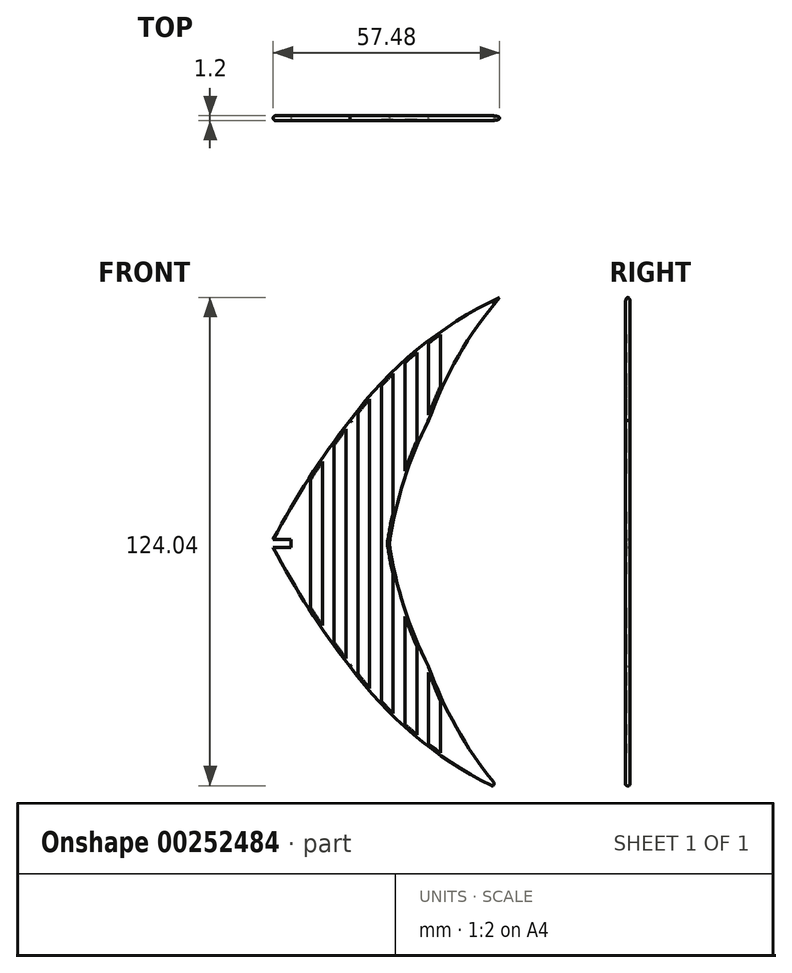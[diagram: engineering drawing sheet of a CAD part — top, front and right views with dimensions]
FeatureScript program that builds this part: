
annotation { "Feature Type Name" : "Feature", "Feature Type Description" : "" }
export const myFeature = defineFeature(function(context is Context, id is Id, definition is map)
    precondition{}
    {
        {
            var Q0;
            Q0=qCreatedBy(makeId("Front.planeOp"),FACE);
            var sketch = newSketch(context, id + "F0", { "sketchPlane" : qUnion([Q0])});
            skLineSegment(sketch, "E0", {"start": v(0, 0) * mm, "end": v(30, 0) * mm});
            skLineSegment(sketch, "E1", {"start": v(20, 31.25) * mm, "end": v(40, 31.25) * mm});
            skPoint(sketch, "E2", {"position": v(58, 62.5) * mm});
            skArc(sketch, "E3", {"start": v(20, 31.25) * mm, "mid": v(9.27, 16.09) * mm, "end": v(0, 0) * mm});
            skArc(sketch, "E4", {"start": v(58, 62.5) * mm, "mid": v(37.05, 49.25) * mm, "end": v(20, 31.25) * mm});
            skArc(sketch, "E5", {"start": v(58, 62.5) * mm, "mid": v(47.58, 47.7) * mm, "end": v(40, 31.25) * mm});
            skArc(sketch, "E6", {"start": v(40, 31.25) * mm, "mid": v(33.7, 16.04) * mm, "end": v(30, 0) * mm});
            skSolve(sketch);
        }
        {
            var Q0;
            Q0=qSketchRegion(id+"F0",true);
            extrude(context, id + "F1", {"entities" : qUnion([Q0]), "endBound" : BoundingType.SYMMETRIC, "depth" : 1.2 * mm});
        }
        {
            var Q0;
            Q0=makeQuery(id+"F1.opExtrude","SWEPT_BODY",BODY,{"disambiguationData":[OSD([sQuery(id+"F0.wireOp",EDGE,"E0"),sQuery(id+"F0.wireOp",EDGE,"E3"),sQuery(id+"F0.wireOp",EDGE,"E4"),sQuery(id+"F0.wireOp",EDGE,"E5"),sQuery(id+"F0.wireOp",EDGE,"E6")])]});
            var Q1;
            Q1=qCreatedBy(makeId("Top.planeOp"),FACE);
            mirror(context, id + "F2", {"operationType" : NewBodyOperationType.ADD, "entities" : qUnion([Q0]), "mirrorPlane" : qUnion([Q1])});
        }
        {
            var Q0;
            Q0=qCreatedBy(makeId("Front.planeOp"),FACE);
            var sketch = newSketch(context, id + "F3", { "sketchPlane" : qUnion([Q0])});
            skLineSegment(sketch, "E7.bottom", {"start": v(5, -1) * mm, "end": v(-5, -1) * mm});
            skLineSegment(sketch, "E7.top", {"start": v(5, 1) * mm, "end": v(-5, 1) * mm});
            skLineSegment(sketch, "E7.left", {"start": v(5, -1) * mm, "end": v(5, 1) * mm});
            skLineSegment(sketch, "E7.right", {"start": v(-5, -1) * mm, "end": v(-5, 1) * mm});
            skPoint(sketch, "E7.middle", {"position": v(0, 0) * mm});
            skSolve(sketch);
        }
        {
            var Q0;
            Q0=makeQuery(id+"F3.imprint","IMPRINT",FACE,{"disambiguationData":[TD([[makeQuery(id+"F3.imprint","IMPRINT",EDGE,{"derivedFrom":sQuery(id+"F3.wireOp",EDGE,"E7.bottom")}),-1.0]])]});
            extrude(context, id + "F4", {"entities" : qUnion([Q0]), "operationType" : NewBodyOperationType.REMOVE, "endBound" : BoundingType.SYMMETRIC, "oppositeDirection" : true, "depth" : 5 * mm});
        }
        {
            var Q0;
            Q0=makeQuery(id+"F1.opExtrude","CAP_EDGE",EDGE,{"disambiguationData":[OSD([sQuery(id+"F0.wireOp",EDGE,"E4")])],"isStart":false});
            var Q1;
            Q1=makeQuery(id+"F1.opExtrude","CAP_EDGE",EDGE,{"disambiguationData":[OSD([sQuery(id+"F0.wireOp",EDGE,"E4")])],"isStart":true});
            var Q2;
            Q2=makeQuery(id+"F1.opExtrude","CAP_EDGE",EDGE,{"disambiguationData":[OSD([sQuery(id+"F0.wireOp",EDGE,"E3")])],"isStart":false});
            var Q3;
            Q3=makeQuery(id+"F1.opExtrude","CAP_EDGE",EDGE,{"disambiguationData":[OSD([sQuery(id+"F0.wireOp",EDGE,"E3")])],"isStart":true});
            var Q4;
            Q4=makeQuery(id+"F1.opExtrude","CAP_EDGE",EDGE,{"disambiguationData":[OSD([sQuery(id+"F0.wireOp",EDGE,"E5")])],"isStart":false});
            var Q5;
            Q5=makeQuery(id+"F1.opExtrude","CAP_EDGE",EDGE,{"disambiguationData":[OSD([sQuery(id+"F0.wireOp",EDGE,"E5")])],"isStart":true});
            var Q6;
            Q6=makeQuery(id+"F1.opExtrude","CAP_EDGE",EDGE,{"disambiguationData":[OSD([sQuery(id+"F0.wireOp",EDGE,"E6")])],"isStart":false});
            var Q7;
            Q7=makeQuery(id+"F1.opExtrude","CAP_EDGE",EDGE,{"disambiguationData":[OSD([sQuery(id+"F0.wireOp",EDGE,"E6")])],"isStart":true});
            var Q8;
            Q8=makeQuery(id+"F2.opPattern","COPY",EDGE,{"derivedFrom":makeQuery(id+"F1.opExtrude","CAP_EDGE",EDGE,{"disambiguationData":[OSD([sQuery(id+"F0.wireOp",EDGE,"E3")])],"isStart":false}),"instanceName":"1"});
            var Q9;
            Q9=makeQuery(id+"F2.opPattern","COPY",EDGE,{"derivedFrom":makeQuery(id+"F1.opExtrude","CAP_EDGE",EDGE,{"disambiguationData":[OSD([sQuery(id+"F0.wireOp",EDGE,"E3")])],"isStart":true}),"instanceName":"1"});
            var Q10;
            Q10=makeQuery(id+"F2.opPattern","COPY",EDGE,{"derivedFrom":makeQuery(id+"F1.opExtrude","CAP_EDGE",EDGE,{"disambiguationData":[OSD([sQuery(id+"F0.wireOp",EDGE,"E4")])],"isStart":false}),"instanceName":"1"});
            var Q11;
            Q11=makeQuery(id+"F2.opPattern","COPY",EDGE,{"derivedFrom":makeQuery(id+"F1.opExtrude","CAP_EDGE",EDGE,{"disambiguationData":[OSD([sQuery(id+"F0.wireOp",EDGE,"E4")])],"isStart":true}),"instanceName":"1"});
            var Q12;
            Q12=makeQuery(id+"F2.opPattern","COPY",EDGE,{"derivedFrom":makeQuery(id+"F1.opExtrude","CAP_EDGE",EDGE,{"disambiguationData":[OSD([sQuery(id+"F0.wireOp",EDGE,"E6")])],"isStart":false}),"instanceName":"1"});
            var Q13;
            Q13=makeQuery(id+"F2.opPattern","COPY",FACE,{"derivedFrom":makeQuery(id+"F1.opExtrude","SWEPT_FACE",FACE,{"disambiguationData":[OSD([sQuery(id+"F0.wireOp",EDGE,"E6")])]}),"instanceName":"1"});
            var Q14;
            Q14=makeQuery(id+"F2.opPattern","COPY",EDGE,{"derivedFrom":makeQuery(id+"F1.opExtrude","CAP_EDGE",EDGE,{"disambiguationData":[OSD([sQuery(id+"F0.wireOp",EDGE,"E5")])],"isStart":false}),"instanceName":"1"});
            var Q15;
            Q15=makeQuery(id+"F2.opPattern","COPY",FACE,{"derivedFrom":makeQuery(id+"F1.opExtrude","SWEPT_FACE",FACE,{"disambiguationData":[OSD([sQuery(id+"F0.wireOp",EDGE,"E5")])]}),"instanceName":"1"});
            fillet(context, id + "F5", {"entities" : qUnion([Q0, Q1, Q2, Q3, Q4, Q5, Q6, Q7, Q8, Q9, Q10, Q11, Q12, Q13, Q14, Q15]), "radius" : 0.5 * mm, "tangentPropagation" : true, "allowEdgeOverflow" : false});
        }
        {
            var Q0;
            {var subQ0=makeQuery(id+"F1.opExtrude","CAP_FACE",FACE,{"disambiguationData":[OSD([sQuery(id+"F0.wireOp",EDGE,"E0"),sQuery(id+"F0.wireOp",EDGE,"E3"),sQuery(id+"F0.wireOp",EDGE,"E4"),sQuery(id+"F0.wireOp",EDGE,"E5"),sQuery(id+"F0.wireOp",EDGE,"E6")])],"isStart":false});Q0=makeQuery(id+"F2.boolean.opBoolean","MERGE",FACE,{"derivedFrom":[subQ0,makeQuery(id+"F2.opPattern","COPY",FACE,{"derivedFrom":subQ0,"instanceName":"1"})]});}
            var sketch = newSketch(context, id + "F6", { "sketchPlane" : qUnion([Q0])});
            skLineSegment(sketch, "E8.bottom", {"start": v(10, -23.87) * mm, "end": v(13, -23.87) * mm});
            skLineSegment(sketch, "E8.top", {"start": v(10, 23.87) * mm, "end": v(13, 23.87) * mm});
            skLineSegment(sketch, "E8.left", {"start": v(10, -23.87) * mm, "end": v(10, 23.87) * mm});
            skLineSegment(sketch, "E8.right", {"start": v(13, -23.87) * mm, "end": v(13, 23.87) * mm});
            skPoint(sketch, "E8.middle", {"position": v(11.5, 0) * mm});
            skLineSegment(sketch, "E9.bottom", {"start": v(19, -36) * mm, "end": v(16, -36) * mm});
            skLineSegment(sketch, "E9.top", {"start": v(19, 36) * mm, "end": v(16, 36) * mm});
            skLineSegment(sketch, "E9.left", {"start": v(19, -36) * mm, "end": v(19, 36) * mm});
            skLineSegment(sketch, "E9.right", {"start": v(16, -36) * mm, "end": v(16, 36) * mm});
            skPoint(sketch, "E9.middle", {"position": v(17.5, 0) * mm});
            skLineSegment(sketch, "E10.bottom", {"start": v(25, -44.67) * mm, "end": v(22, -44.67) * mm});
            skLineSegment(sketch, "E10.top", {"start": v(25, 44.67) * mm, "end": v(22, 44.67) * mm});
            skLineSegment(sketch, "E10.left", {"start": v(25, -44.67) * mm, "end": v(25, 44.67) * mm});
            skLineSegment(sketch, "E10.right", {"start": v(22, -44.67) * mm, "end": v(22, 44.67) * mm});
            skPoint(sketch, "E10.middle", {"position": v(23.5, 0) * mm});
            skLineSegment(sketch, "E11.bottom", {"start": v(31, -52.22) * mm, "end": v(28, -52.22) * mm});
            skLineSegment(sketch, "E11.top", {"start": v(31, 52.22) * mm, "end": v(28, 52.22) * mm});
            skLineSegment(sketch, "E11.left", {"start": v(31, -52.22) * mm, "end": v(31, 52.22) * mm});
            skLineSegment(sketch, "E11.right", {"start": v(28, -52.22) * mm, "end": v(28, 52.22) * mm});
            skPoint(sketch, "E11.middle", {"position": v(29.5, 0) * mm});
            skLineSegment(sketch, "E12.bottom", {"start": v(37, -58.76) * mm, "end": v(34, -58.76) * mm});
            skLineSegment(sketch, "E12.top", {"start": v(37, 58.76) * mm, "end": v(34, 58.76) * mm});
            skLineSegment(sketch, "E12.left", {"start": v(37, -58.76) * mm, "end": v(37, 58.76) * mm});
            skLineSegment(sketch, "E12.right", {"start": v(34, -58.76) * mm, "end": v(34, 58.76) * mm});
            skPoint(sketch, "E12.middle", {"position": v(35.5, 0) * mm});
            skLineSegment(sketch, "E13.bottom", {"start": v(43, -59.41) * mm, "end": v(40, -59.41) * mm});
            skLineSegment(sketch, "E13.top", {"start": v(43, 59.41) * mm, "end": v(40, 59.41) * mm});
            skLineSegment(sketch, "E13.left", {"start": v(43, -59.41) * mm, "end": v(43, 59.41) * mm});
            skLineSegment(sketch, "E13.right", {"start": v(40, -59.41) * mm, "end": v(40, 59.41) * mm});
            skPoint(sketch, "E13.middle", {"position": v(41.5, 0) * mm});
            skSolve(sketch);
        }
        {
            var Q0;
            {var subQ0=sQuery(id+"F6.wireOp",EDGE,"E8.left");var subQ1=sQuery(id+"F0.wireOp",EDGE,"E3");var subQ2=makeQuery(id+"F1.opExtrude","CAP_FACE",FACE,{"disambiguationData":[OSD([sQuery(id+"F0.wireOp",EDGE,"E0"),subQ1,sQuery(id+"F0.wireOp",EDGE,"E4"),sQuery(id+"F0.wireOp",EDGE,"E5"),sQuery(id+"F0.wireOp",EDGE,"E6")])],"isStart":false});var subQ3=makeQuery(id+"F2.boolean.opBoolean","MERGE",FACE,{"derivedFrom":[subQ2,makeQuery(id+"F2.opPattern","COPY",FACE,{"derivedFrom":subQ2,"instanceName":"1"})]});var subQ4=makeQuery(id+"F1.opExtrude","CAP_EDGE",EDGE,{"disambiguationData":[OSD([subQ1])],"isStart":false});var subQ5=makeQuery(id+"F5.opFillet","BLEND_EDGE",EDGE,{"blendedFrom":[makeQuery(id+"F2.opPattern","COPY",EDGE,{"derivedFrom":subQ4,"instanceName":"1"}),subQ3],"blendedInto":[subQ3]});var subQ6=makeQuery(id+"F6.imprint","INTERSECT",VERTEX,{"derivedFrom":[subQ5,subQ0]});Q0=makeQuery(id+"F6.imprint","IMPRINT",FACE,{"disambiguationData":[TD([[makeQuery(id+"F6.imprint","IMPRINT",EDGE,{"disambiguationData":[TD([[subQ6,-1.0]])],"derivedFrom":subQ0}),-1.0]])]});}
            var Q1;
            {var subQ0=sQuery(id+"F6.wireOp",EDGE,"E9.left");var subQ1=sQuery(id+"F0.wireOp",EDGE,"E3");var subQ2=makeQuery(id+"F1.opExtrude","CAP_FACE",FACE,{"disambiguationData":[OSD([sQuery(id+"F0.wireOp",EDGE,"E0"),subQ1,sQuery(id+"F0.wireOp",EDGE,"E4"),sQuery(id+"F0.wireOp",EDGE,"E5"),sQuery(id+"F0.wireOp",EDGE,"E6")])],"isStart":false});var subQ3=makeQuery(id+"F2.boolean.opBoolean","MERGE",FACE,{"derivedFrom":[subQ2,makeQuery(id+"F2.opPattern","COPY",FACE,{"derivedFrom":subQ2,"instanceName":"1"})]});var subQ4=makeQuery(id+"F1.opExtrude","CAP_EDGE",EDGE,{"disambiguationData":[OSD([subQ1])],"isStart":false});var subQ5=makeQuery(id+"F5.opFillet","BLEND_EDGE",EDGE,{"blendedFrom":[makeQuery(id+"F2.opPattern","COPY",EDGE,{"derivedFrom":subQ4,"instanceName":"1"}),subQ3],"blendedInto":[subQ3]});var subQ6=makeQuery(id+"F6.imprint","INTERSECT",VERTEX,{"derivedFrom":[subQ5,subQ0]});Q1=makeQuery(id+"F6.imprint","IMPRINT",FACE,{"disambiguationData":[TD([[makeQuery(id+"F6.imprint","IMPRINT",EDGE,{"disambiguationData":[TD([[subQ6,-1.0]])],"derivedFrom":subQ0}),1.0]])]});}
            var Q2;
            {var subQ0=sQuery(id+"F6.wireOp",EDGE,"E10.left");var subQ1=sQuery(id+"F0.wireOp",EDGE,"E4");var subQ2=makeQuery(id+"F1.opExtrude","CAP_FACE",FACE,{"disambiguationData":[OSD([sQuery(id+"F0.wireOp",EDGE,"E0"),sQuery(id+"F0.wireOp",EDGE,"E3"),subQ1,sQuery(id+"F0.wireOp",EDGE,"E5"),sQuery(id+"F0.wireOp",EDGE,"E6")])],"isStart":false});var subQ3=makeQuery(id+"F2.boolean.opBoolean","MERGE",FACE,{"derivedFrom":[subQ2,makeQuery(id+"F2.opPattern","COPY",FACE,{"derivedFrom":subQ2,"instanceName":"1"})]});var subQ4=makeQuery(id+"F1.opExtrude","CAP_EDGE",EDGE,{"disambiguationData":[OSD([subQ1])],"isStart":false});var subQ5=makeQuery(id+"F5.opFillet","BLEND_EDGE",EDGE,{"blendedFrom":[makeQuery(id+"F2.opPattern","COPY",EDGE,{"derivedFrom":subQ4,"instanceName":"1"}),subQ3],"blendedInto":[subQ3]});var subQ6=makeQuery(id+"F6.imprint","INTERSECT",VERTEX,{"derivedFrom":[subQ5,subQ0]});Q2=makeQuery(id+"F6.imprint","IMPRINT",FACE,{"disambiguationData":[TD([[makeQuery(id+"F6.imprint","IMPRINT",EDGE,{"disambiguationData":[TD([[subQ6,-1.0]])],"derivedFrom":subQ0}),1.0]])]});}
            var Q3;
            {var subQ0=sQuery(id+"F0.wireOp",EDGE,"E6");var subQ1=sQuery(id+"F0.wireOp",EDGE,"E4");var subQ2=sQuery(id+"F0.wireOp",EDGE,"E0");var subQ3=makeQuery(id+"F1.opExtrude","CAP_FACE",FACE,{"disambiguationData":[OSD([subQ2,sQuery(id+"F0.wireOp",EDGE,"E3"),subQ1,sQuery(id+"F0.wireOp",EDGE,"E5"),subQ0])],"isStart":false});var subQ4=makeQuery(id+"F2.boolean.opBoolean","MERGE",FACE,{"derivedFrom":[subQ3,makeQuery(id+"F2.opPattern","COPY",FACE,{"derivedFrom":subQ3,"instanceName":"1"})]});var subQ5=makeQuery(id+"F1.opExtrude","CAP_VERTEX",VERTEX,{"disambiguationData":[OSD([subQ2,subQ0])],"isStart":false});var subQ6=makeQuery(id+"F5.opFillet","BLEND_EDGE",EDGE,{"blendedFrom":[makeQuery(id+"F2.boolean.opBoolean","MERGE",VERTEX,{"derivedFrom":[subQ5,makeQuery(id+"F2.opPattern","COPY",VERTEX,{"derivedFrom":subQ5,"instanceName":"1"})]}),subQ4],"blendedInto":[subQ4]});Q3=makeQuery(id+"F6.imprint","IMPRINT",FACE,{"disambiguationData":[TD([[makeQuery(id+"F6.imprint","IMPRINT",EDGE,{"derivedFrom":subQ6}),-1.0]])]});}
            var Q4;
            {var subQ0=sQuery(id+"F6.wireOp",EDGE,"E12.left");var subQ1=sQuery(id+"F0.wireOp",EDGE,"E6");var subQ2=sQuery(id+"F0.wireOp",EDGE,"E4");var subQ3=makeQuery(id+"F1.opExtrude","CAP_FACE",FACE,{"disambiguationData":[OSD([sQuery(id+"F0.wireOp",EDGE,"E0"),sQuery(id+"F0.wireOp",EDGE,"E3"),subQ2,sQuery(id+"F0.wireOp",EDGE,"E5"),subQ1])],"isStart":false});var subQ4=makeQuery(id+"F2.boolean.opBoolean","MERGE",FACE,{"derivedFrom":[subQ3,makeQuery(id+"F2.opPattern","COPY",FACE,{"derivedFrom":subQ3,"instanceName":"1"})]});var subQ5=makeQuery(id+"F5.opFillet","BLEND_EDGE",EDGE,{"blendedFrom":[makeQuery(id+"F1.opExtrude","CAP_EDGE",EDGE,{"disambiguationData":[OSD([subQ2])],"isStart":false}),subQ4],"blendedInto":[subQ4]});var subQ6=makeQuery(id+"F6.imprint","INTERSECT",VERTEX,{"derivedFrom":[subQ5,subQ0]});Q4=makeQuery(id+"F6.imprint","IMPRINT",FACE,{"disambiguationData":[TD([[makeQuery(id+"F6.imprint","IMPRINT",EDGE,{"disambiguationData":[TD([[subQ6,1.0]])],"derivedFrom":subQ0}),1.0]])]});}
            var Q5;
            {var subQ0=sQuery(id+"F6.wireOp",EDGE,"E12.left");var subQ1=sQuery(id+"F0.wireOp",EDGE,"E6");var subQ2=sQuery(id+"F0.wireOp",EDGE,"E4");var subQ3=makeQuery(id+"F1.opExtrude","CAP_FACE",FACE,{"disambiguationData":[OSD([sQuery(id+"F0.wireOp",EDGE,"E0"),sQuery(id+"F0.wireOp",EDGE,"E3"),subQ2,sQuery(id+"F0.wireOp",EDGE,"E5"),subQ1])],"isStart":false});var subQ4=makeQuery(id+"F2.boolean.opBoolean","MERGE",FACE,{"derivedFrom":[subQ3,makeQuery(id+"F2.opPattern","COPY",FACE,{"derivedFrom":subQ3,"instanceName":"1"})]});var subQ5=makeQuery(id+"F5.opFillet","BLEND_EDGE",EDGE,{"blendedFrom":[makeQuery(id+"F2.opPattern","COPY",EDGE,{"derivedFrom":makeQuery(id+"F1.opExtrude","CAP_EDGE",EDGE,{"disambiguationData":[OSD([subQ2])],"isStart":false}),"instanceName":"1"}),subQ4],"blendedInto":[subQ4]});var subQ6=makeQuery(id+"F6.imprint","INTERSECT",VERTEX,{"derivedFrom":[subQ5,subQ0]});Q5=makeQuery(id+"F6.imprint","IMPRINT",FACE,{"disambiguationData":[TD([[makeQuery(id+"F6.imprint","IMPRINT",EDGE,{"disambiguationData":[TD([[subQ6,-1.0]])],"derivedFrom":subQ0}),1.0]])]});}
            var Q6;
            {var subQ0=sQuery(id+"F6.wireOp",EDGE,"E13.left");var subQ1=sQuery(id+"F0.wireOp",EDGE,"E5");var subQ2=sQuery(id+"F0.wireOp",EDGE,"E4");var subQ3=makeQuery(id+"F1.opExtrude","CAP_FACE",FACE,{"disambiguationData":[OSD([sQuery(id+"F0.wireOp",EDGE,"E0"),sQuery(id+"F0.wireOp",EDGE,"E3"),subQ2,subQ1,sQuery(id+"F0.wireOp",EDGE,"E6")])],"isStart":false});var subQ4=makeQuery(id+"F2.boolean.opBoolean","MERGE",FACE,{"derivedFrom":[subQ3,makeQuery(id+"F2.opPattern","COPY",FACE,{"derivedFrom":subQ3,"instanceName":"1"})]});var subQ5=makeQuery(id+"F5.opFillet","BLEND_EDGE",EDGE,{"blendedFrom":[makeQuery(id+"F1.opExtrude","CAP_EDGE",EDGE,{"disambiguationData":[OSD([subQ1])],"isStart":false}),subQ4],"blendedInto":[subQ4]});var subQ6=makeQuery(id+"F6.imprint","INTERSECT",VERTEX,{"derivedFrom":[subQ5,subQ0]});Q6=makeQuery(id+"F6.imprint","IMPRINT",FACE,{"disambiguationData":[TD([[makeQuery(id+"F6.imprint","IMPRINT",EDGE,{"disambiguationData":[TD([[subQ6,-1.0]])],"derivedFrom":subQ0}),1.0]])]});}
            var Q7;
            {var subQ0=sQuery(id+"F6.wireOp",EDGE,"E13.left");var subQ1=sQuery(id+"F0.wireOp",EDGE,"E5");var subQ2=sQuery(id+"F0.wireOp",EDGE,"E4");var subQ3=makeQuery(id+"F1.opExtrude","CAP_FACE",FACE,{"disambiguationData":[OSD([sQuery(id+"F0.wireOp",EDGE,"E0"),sQuery(id+"F0.wireOp",EDGE,"E3"),subQ2,subQ1,sQuery(id+"F0.wireOp",EDGE,"E6")])],"isStart":false});var subQ4=makeQuery(id+"F2.boolean.opBoolean","MERGE",FACE,{"derivedFrom":[subQ3,makeQuery(id+"F2.opPattern","COPY",FACE,{"derivedFrom":subQ3,"instanceName":"1"})]});var subQ5=makeQuery(id+"F5.opFillet","BLEND_EDGE",EDGE,{"blendedFrom":[makeQuery(id+"F2.opPattern","COPY",EDGE,{"derivedFrom":makeQuery(id+"F1.opExtrude","CAP_EDGE",EDGE,{"disambiguationData":[OSD([subQ2])],"isStart":false}),"instanceName":"1"}),subQ4],"blendedInto":[subQ4]});var subQ6=makeQuery(id+"F6.imprint","INTERSECT",VERTEX,{"derivedFrom":[subQ5,subQ0]});Q7=makeQuery(id+"F6.imprint","IMPRINT",FACE,{"disambiguationData":[TD([[makeQuery(id+"F6.imprint","IMPRINT",EDGE,{"disambiguationData":[TD([[subQ6,-1.0]])],"derivedFrom":subQ0}),1.0]])]});}
            extrude(context, id + "F7", {"entities" : qUnion([Q0, Q1, Q2, Q3, Q4, Q5, Q6, Q7]), "operationType" : NewBodyOperationType.REMOVE, "oppositeDirection" : true, "depth" : 0.2 * mm});
        }
    });
